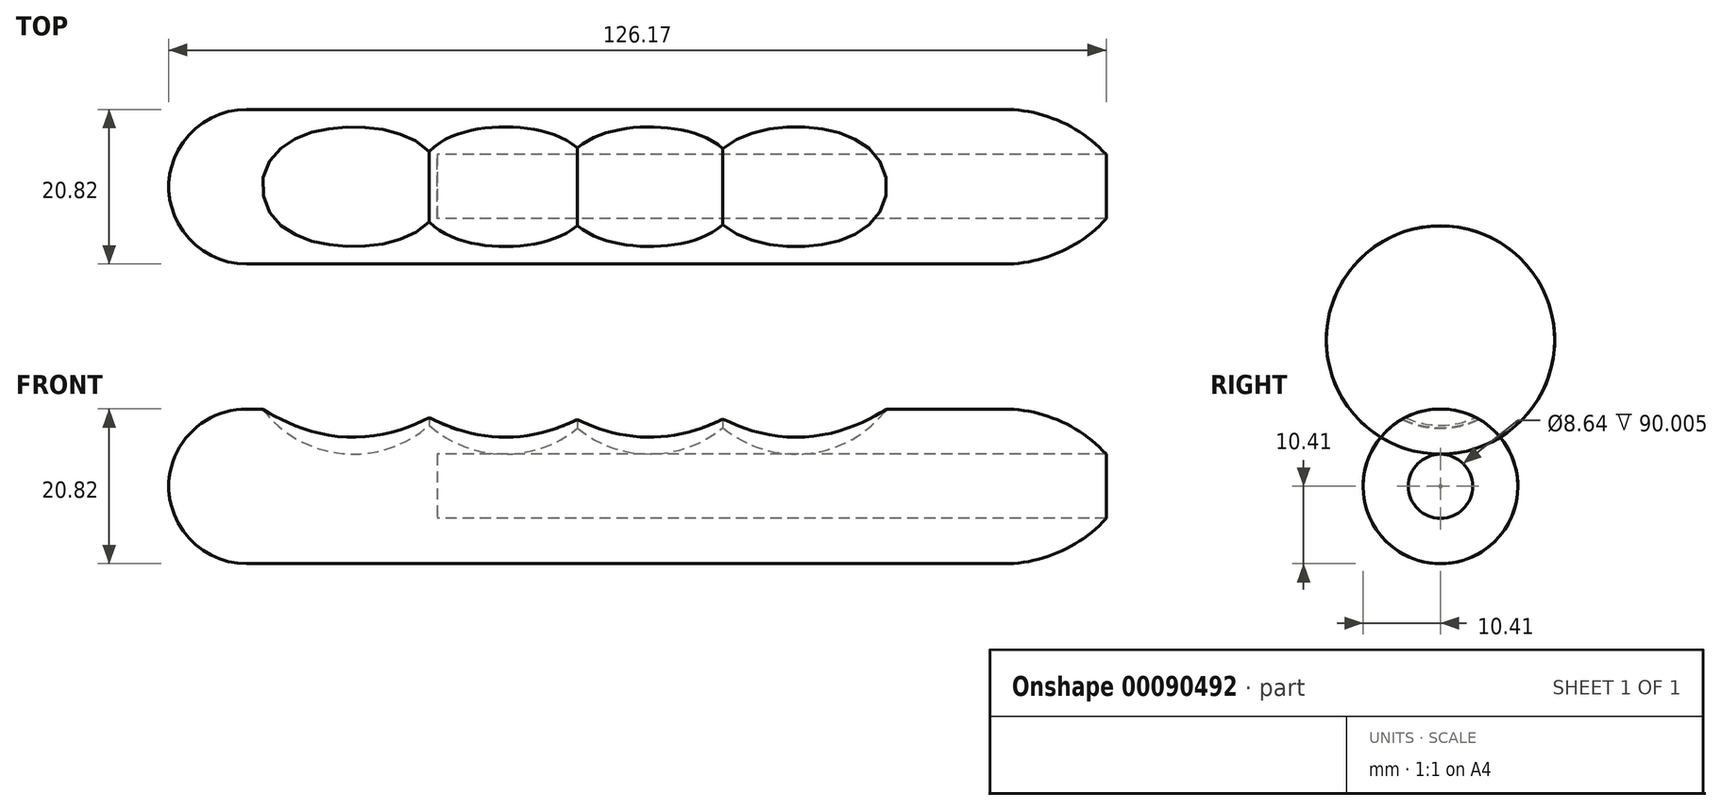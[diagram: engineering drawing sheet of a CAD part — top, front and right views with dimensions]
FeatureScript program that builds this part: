
annotation { "Feature Type Name" : "Feature", "Feature Type Description" : "" }
export const myFeature = defineFeature(function(context is Context, id is Id, definition is map)
    precondition{}
    {
        {
            var Q0;
            Q0=qCreatedBy(makeId("Front.planeOp"),FACE);
            var sketch = newSketch(context, id + "F0", { "sketchPlane" : qUnion([Q0])});
            skLineSegment(sketch, "E0", {"start": v(0, 10.4) * mm, "end": v(-101.85, 10.4) * mm});
            skArc(sketch, "E1", {"start": v(0, 10.4) * mm, "mid": v(9.86, 7.6) * mm, "end": v(16.76, 0) * mm});
            skArc(sketch, "E2", {"start": v(-101.85, 10.4) * mm, "mid": v(-109.24, 7.36) * mm, "end": v(-112.36, 0) * mm});
            skLineSegment(sketch, "E3", {"start": v(16.76, 0) * mm, "end": v(-112.36, 0) * mm});
            skSolve(sketch);
        }
        {
            var Q0;
            Q0=makeQuery(id+"F0.imprint","IMPRINT",FACE,{"disambiguationData":[TD([[makeQuery(id+"F0.imprint","IMPRINT",EDGE,{"derivedFrom":sQuery(id+"F0.wireOp",EDGE,"E0")}),1.0]])]});
            var Q1;
            Q1=sQuery(id+"F0.wireOp",EDGE,"E3");
            revolve(context, id + "F1", {"entities" : qUnion([Q0]), "axis" : qUnion([Q1]), "revolveType" : RevolveType.ONE_DIRECTION, "angle" : 360 * degree});
        }
        {
            var Q0;
            Q0=qCreatedBy(makeId("Front.planeOp"),FACE);
            var sketch = newSketch(context, id + "F2", { "sketchPlane" : qUnion([Q0])});
            skArc(sketch, "E4", {"start": v(-77.28, 31.17) * mm, "mid": v(-93.79, 33.71) * mm, "end": v(-102.86, 19.7) * mm});
            skArc(sketch, "E5", {"start": v(-12.57, 19.7) * mm, "mid": v(-21.42, 33.6) * mm, "end": v(-37.77, 31.48) * mm});
            skLineSegment(sketch, "E6", {"start": v(-87.5, 19.7) * mm, "end": v(-87.5, 19.7) * mm});
            skLineSegment(sketch, "E7", {"start": v(-87.5, 19.7) * mm, "end": v(-27.93, 19.7) * mm});
            skArc(sketch, "E8.trimOffspring", {"start": v(-57.35, 31.59) * mm, "mid": v(-67.4, 35.05) * mm, "end": v(-77.28, 31.17) * mm});
            skArc(sketch, "E9.trimOffspring", {"start": v(-37.77, 31.48) * mm, "mid": v(-47.54, 35.05) * mm, "end": v(-57.35, 31.59) * mm});
            skLineSegment(sketch, "E10", {"start": v(-102.86, 19.7) * mm, "end": v(-12.57, 19.7) * mm});
            skSolve(sketch);
        }
        {
            var Q0;
            Q0=makeQuery(id+"F2.imprint","IMPRINT",FACE,{"disambiguationData":[TD([[makeQuery(id+"F2.imprint","IMPRINT",EDGE,{"derivedFrom":sQuery(id+"F2.wireOp",EDGE,"E4")}),1.0]])]});
            var Q1;
            Q1=sQuery(id+"F2.wireOp",EDGE,"E4");
            var Q2;
            Q2=sQuery(id+"F2.wireOp",EDGE,"E8.trimOffspring");
            var Q3;
            Q3=sQuery(id+"F2.wireOp",EDGE,"25aa9bdd-a1c3-45c1-9293-d6c39c4f945d");
            var Q4;
            Q4=sQuery(id+"F2.wireOp",EDGE,"8dac002a-1f2d-472e-b4c1-590d953e38d2");
            var Q5;
            Q5=sQuery(id+"F2.wireOp",EDGE,"E5");
            var Q6;
            Q6=sQuery(id+"F2.wireOp",EDGE,"E9.trimOffspring");
            var Q7;
            Q7=sQuery(id+"F2.wireOp",EDGE,"E7");
            revolve(context, id + "F3", {"operationType" : NewBodyOperationType.REMOVE, "entities" : qUnion([Q0]), "surfaceEntities" : qUnion([Q1, Q2, Q3, Q4, Q5, Q6]), "axis" : qUnion([Q7]), "revolveType" : RevolveType.ONE_DIRECTION, "angle" : 360 * degree});
        }
        {
            var Q0;
            Q0=qCreatedBy(makeId("Right.planeOp"),FACE);
            cPlane(context, id + "F4", {"entities" : qUnion([Q0]), "cplaneType" : CPlaneType.OFFSET, "offset" : 76.2 * mm, "oppositeDirection" : true, "width" : 152.4 * mm, "height" : 152.4 * mm});
        }
        {
            var Q0;
            Q0=qCreatedBy(id+"F4.planeOp",FACE);
            var sketch = newSketch(context, id + "F5", { "sketchPlane" : qUnion([Q0])});
            skPoint(sketch, "E11", {"position": v(0, 0) * mm});
            skSolve(sketch);
        }
        {
            var Q0;
            Q0=sQuery(id+"F5.wireOp",VERTEX,"E11");
            var Q1;
            Q1=makeQuery(id+"F1.opRevolve","SWEPT_BODY",BODY,{"disambiguationData":[OSD([sQuery(id+"F0.wireOp",EDGE,"E0"),sQuery(id+"F0.wireOp",EDGE,"E1"),sQuery(id+"F0.wireOp",EDGE,"E2"),sQuery(id+"F0.wireOp",EDGE,"E3")])]});
            hole(context, id + "F6", {"style" : HoleStyle.SIMPLE, "endStyle" : HoleEndStyle.THROUGH, "oppositeDirection" : true, "holeDiameter" : 8.64 * mm, "locations" : qUnion([Q0]), "scope" : qUnion([Q1]), "isTappedThrough" : true});
        }
    });
